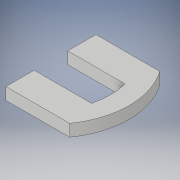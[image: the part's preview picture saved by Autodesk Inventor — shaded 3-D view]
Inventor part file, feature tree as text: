
AUTODESK INVENTOR PART (.ipt)
format: ipt  version: 2019 (Build 230136000, 136)  size: 108,544 bytes
history: native  units: mm
features: extrude x2, sketch x2, other x1
ambient origin geometry x8: Origin, YZ Plane, XZ Plane, XY Plane, X Axis, Y Axis, Z Axis, Center Point
bodies: Body1 (feature_tree)
feature tree (5):
  other  "Твердое тело1"
  extrude  "Выдавливание1"  Depth=5.309mm
  extrude  "Выдавливание2"  Depth=7.5mm
  sketch  "Эскиз1"
  sketch  "Эскиз2"
